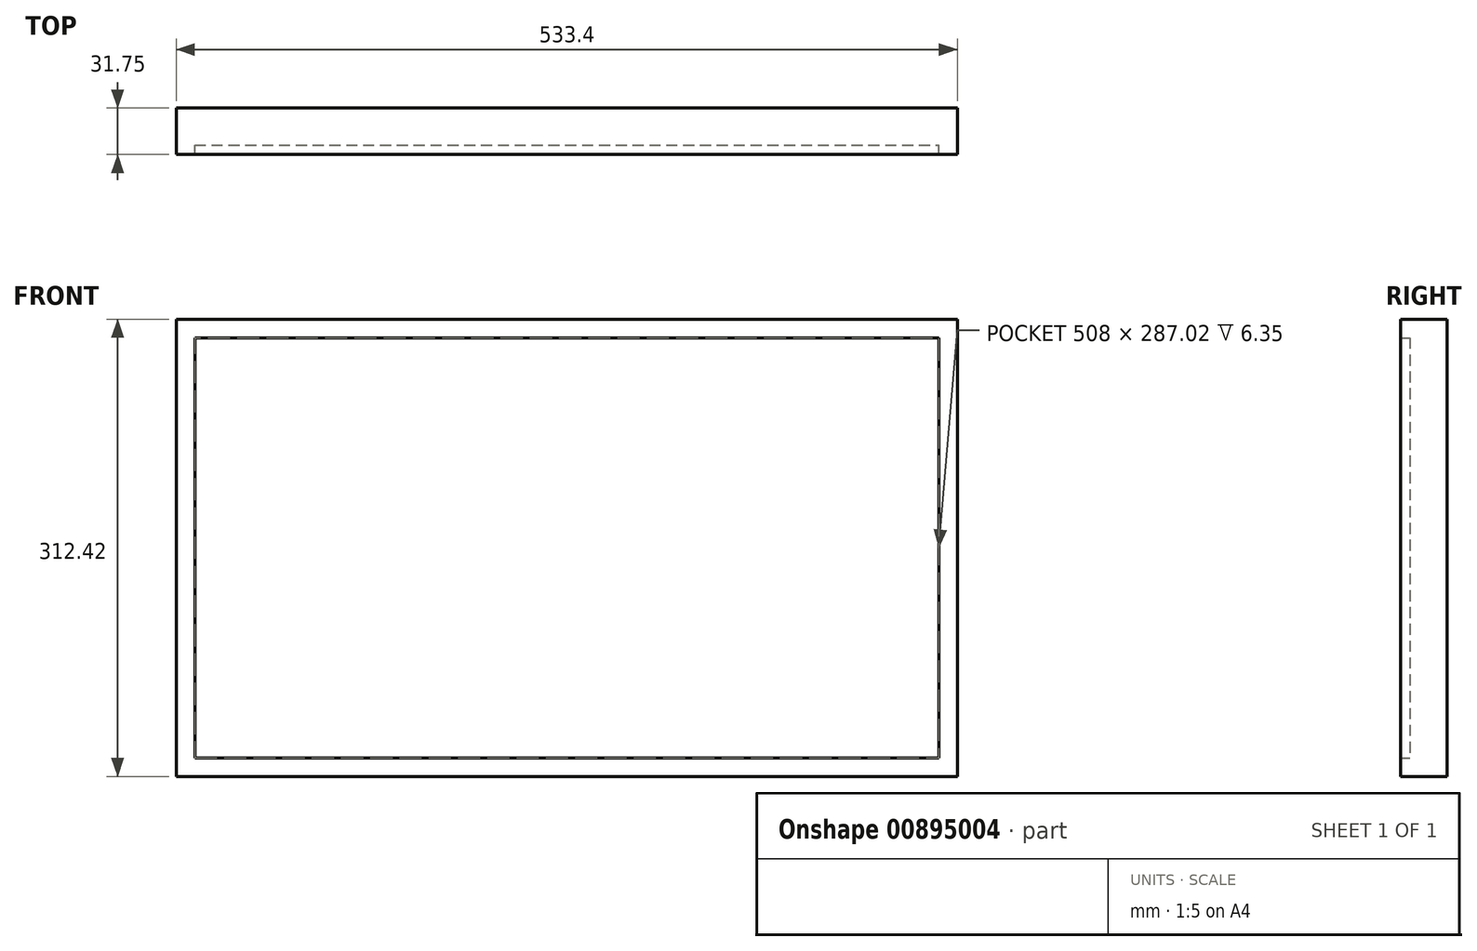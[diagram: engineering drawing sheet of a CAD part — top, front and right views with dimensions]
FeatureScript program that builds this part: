
annotation { "Feature Type Name" : "Feature", "Feature Type Description" : "" }
export const myFeature = defineFeature(function(context is Context, id is Id, definition is map)
    precondition{}
    {
        {
            var Q0;
            Q0=qCreatedBy(makeId("Front.planeOp"),FACE);
            var sketch = newSketch(context, id + "F0", { "sketchPlane" : qUnion([Q0])});
            skLineSegment(sketch, "E0.bottom", {"start": v(-254, 143.51) * mm, "end": v(254, 143.51) * mm});
            skLineSegment(sketch, "E0.top", {"start": v(-254, -143.51) * mm, "end": v(254, -143.51) * mm});
            skLineSegment(sketch, "E0.left", {"start": v(-254, 143.51) * mm, "end": v(-254, -143.5) * mm});
            skLineSegment(sketch, "E0.right", {"start": v(254, 143.51) * mm, "end": v(254, -143.5) * mm});
            skPoint(sketch, "E0.middle", {"position": v(0, 0) * mm});
            skSolve(sketch);
        }
        {
            var Q0;
            Q0=makeQuery(id+"F0.imprint","IMPRINT",FACE,{"disambiguationData":[TD([[makeQuery(id+"F0.imprint","IMPRINT",EDGE,{"derivedFrom":sQuery(id+"F0.wireOp",EDGE,"E0.bottom")}),-1.0]])]});
            extrude(context, id + "F1", {"entities" : qUnion([Q0]), "depth" : 25.4 * mm, "offsetDistance" : 25.4 * mm});
        }
        {
            var Q0;
            Q0=qCreatedBy(makeId("Front.planeOp"),FACE);
            var sketch = newSketch(context, id + "F2", { "sketchPlane" : qUnion([Q0])});
            skLineSegment(sketch, "E1.bottom", {"start": v(-266.7, 156.21) * mm, "end": v(266.7, 156.21) * mm});
            skLineSegment(sketch, "E1.top", {"start": v(-266.7, -156.21) * mm, "end": v(266.7, -156.21) * mm});
            skLineSegment(sketch, "E1.left", {"start": v(-266.7, 156.21) * mm, "end": v(-266.7, -156.21) * mm});
            skLineSegment(sketch, "E1.right", {"start": v(266.7, 156.21) * mm, "end": v(266.7, -156.21) * mm});
            skPoint(sketch, "E1.middle", {"position": v(0, 0) * mm});
            skLineSegment(sketch, "E2.0.0", {"start": v(254, 143.51) * mm, "end": v(-254, 143.51) * mm});
            skLineSegment(sketch, "E2.0.1", {"start": v(-254, 143.51) * mm, "end": v(-254, -143.51) * mm});
            skLineSegment(sketch, "E2.0.2", {"start": v(-254, -143.51) * mm, "end": v(254, -143.51) * mm});
            skLineSegment(sketch, "E2.0.3", {"start": v(254, -143.51) * mm, "end": v(254, 143.51) * mm});
            skSolve(sketch);
        }
        {
            var Q0;
            Q0=qSketchRegion(id+"F2",true);
            extrude(context, id + "F3", {"entities" : qUnion([Q0]), "operationType" : NewBodyOperationType.ADD, "depth" : 31.75 * mm, "offsetDistance" : 25.4 * mm});
        }
    });
